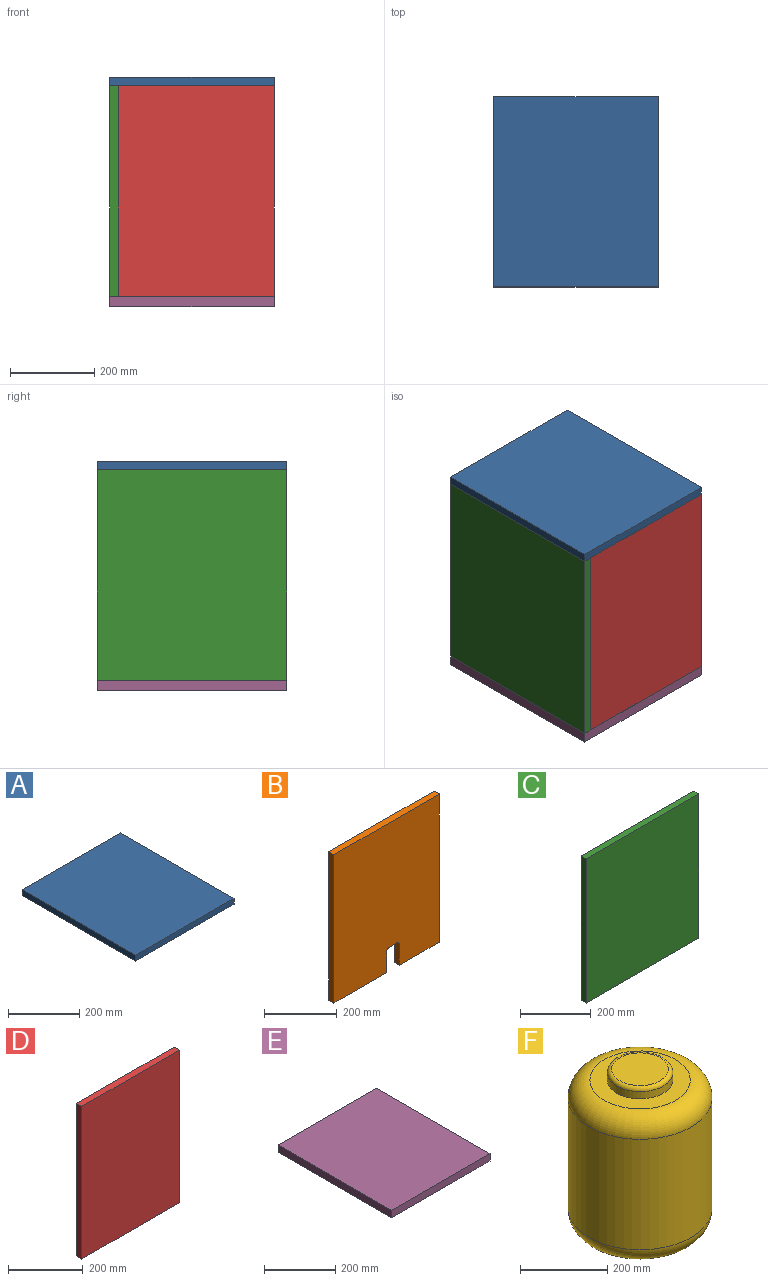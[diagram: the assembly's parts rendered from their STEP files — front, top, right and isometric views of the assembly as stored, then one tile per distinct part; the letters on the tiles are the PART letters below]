
ASSEMBLY  parts=6 mates=5
PART A: 6 faces, bbox 390x450x20 mm
  f0: plane 450x390mm, normal (0,0,1), area 175500mm2, adj f2,f3,f4,f5
  f1: plane 450x390mm, normal (0,0,-1), area 175500mm2, adj f2,f3,f4,f5
  f2: plane 450x20mm, normal (-1,0,0), area 9000mm2, adj f0,f1,f3,f5
  f3: plane 390x20mm, normal (0,1,0), area 7800mm2, adj f0,f1,f2,f4
  f4: plane 450x20mm, normal (1,0,0), area 9000mm2, adj f0,f1,f3,f5
  f5: plane 390x20mm, normal (0,-1,0), area 7800mm2, adj f0,f1,f2,f4
PART B: 12 faces, bbox 410x20x500 mm
  f0: plane 155x20mm, normal (0,0,-1), area 3100mm2, adj f2,f3,f5,f11
  f1: plane 410x20mm, normal (0,0,1), area 8200mm2, adj f2,f3,f10,f11
  f2: plane 500x410mm, normal (0,-1,0), area 201042.9mm2, adj f0,f1,f4,f5,f6,f7,f8,f9
  f3: plane 500x410mm, normal (0,1,0), area 201042.9mm2, adj f0,f1,f4,f5,f6,f7,f8,f9
  f4: plane 205x20mm, normal (0,0,-1), area 4100mm2, adj f2,f3,f7,f10
  f5: plane 70x20mm, normal (-1,0,0), area 1400mm2, adj f0,f2,f3,f8
  f6: plane 30x20mm, normal (0,0,-1), area 600mm2, adj f2,f3,f8,f9
  f7: plane 70x20mm, normal (1,0,0), area 1400mm2, adj f2,f3,f4,f9
  f8: cylinder r=10mm len=20mm, axis (0,-1,0), area 314.2mm2, adj f2,f3,f5,f6
  f9: cylinder r=10mm len=20mm, axis (0,1,0), area 314.2mm2, adj f2,f3,f6,f7
  f10: plane 500x20mm, normal (-1,0,0), area 10000mm2, adj f1,f2,f3,f4
  f11: plane 500x20mm, normal (1,0,0), area 10000mm2, adj f0,f1,f2,f3
PART C: 6 faces, bbox 450x20x500 mm
  f0: plane 450x20mm, normal (0,0,-1), area 9000mm2, adj f2,f3,f4,f5
  f1: plane 450x20mm, normal (0,0,1), area 9000mm2, adj f2,f3,f4,f5
  f2: plane 500x450mm, normal (0,-1,0), area 225000mm2, adj f0,f1,f4,f5
  f3: plane 500x450mm, normal (0,1,0), area 225000mm2, adj f0,f1,f4,f5
  f4: plane 500x20mm, normal (-1,0,0), area 10000mm2, adj f0,f1,f2,f3
  f5: plane 500x20mm, normal (1,0,0), area 10000mm2, adj f0,f1,f2,f3
PART D: 6 faces, bbox 370x20x500 mm
  f0: plane 370x20mm, normal (0,0,1), area 7400mm2, adj f1,f3,f4,f5
  f1: plane 500x20mm, normal (-1,0,0), area 10000mm2, adj f0,f2,f3,f4
  f2: plane 370x20mm, normal (0,0,-1), area 7400mm2, adj f1,f3,f4,f5
  f3: plane 500x370mm, normal (0,-1,0), area 185000mm2, adj f0,f1,f2,f5
  f4: plane 500x370mm, normal (0,1,0), area 185000mm2, adj f0,f1,f2,f5
  f5: plane 500x20mm, normal (1,0,0), area 10000mm2, adj f0,f2,f3,f4
PART E: 6 faces, bbox 390x450x25 mm
  f0: plane 450x390mm, normal (0,0,1), area 175500mm2, adj f2,f3,f4,f5
  f1: plane 450x390mm, normal (0,0,-1), area 175500mm2, adj f2,f3,f4,f5
  f2: plane 450x25mm, normal (-1,0,0), area 11250mm2, adj f0,f1,f3,f5
  f3: plane 390x25mm, normal (0,1,0), area 9750mm2, adj f0,f1,f2,f4
  f4: plane 450x25mm, normal (1,0,0), area 11250mm2, adj f0,f1,f3,f5
  f5: plane 390x25mm, normal (0,-1,0), area 9750mm2, adj f0,f1,f2,f4
PART F: 8 faces, bbox 357.2x357.2x440 mm
  f0: cylinder r=165mm len=330mm, axis (0,0,-1), area 321384.9mm2, adj f3,f4
  f1: plane 230x230mm, normal (0,0,1), area 23876.1mm2, adj f4,f5
  f2: plane 230x230mm, normal (0,0,-1), area 41547.6mm2, adj f3
  f3: torus R=115mm, axis (0,0,1), area 72458.2mm2, adj f0,f2
  f4: torus R=115mm, axis (0,0,1), area 72458.2mm2, adj f0,f1
  f5: cylinder r=75mm len=150mm, axis (0,0,-1), area 9424.8mm2, adj f1,f7
  f6: plane 130x130mm, normal (0,0,1), area 13273.2mm2, adj f7
  f7: torus R=65mm, axis (0,0,1), area 7043.6mm2, adj f5,f6
PLACE A t=(612.76,384.78,189.24)mm
PLACE B rot(axis=(0,0,-1),90deg) t=(983.2,827.64,-268.93)mm
PLACE C rot(axis=(0,0,-1),90deg) t=(613.2,820.61,-256.79)mm
PLACE D t=(593.04,446.65,-243.62)mm
PLACE E t=(612.76,384.78,-335.76)mm
PLACE F t=(805.41,640.49,-310.76)mm
MATE fastened B.f3 <-> D.f5  axis (1,0,0) through (983.2,446.65,-310.76)mm
MATE fastened E.f0 <-> C.f0  axis (0,0,1) through (593.2,876.65,-310.76)mm
MATE fastened A.f1 <-> C.f1  axis (0,0,-1) through (593.2,876.65,189.24)mm
MATE fastened D.f2 <-> E.f0  axis (0,0,-1) through (983.2,426.65,-310.76)mm
MATE fastened F.f0 <-> E.f0  axis (0,0,-1) through (788.2,651.65,-310.76)mm
